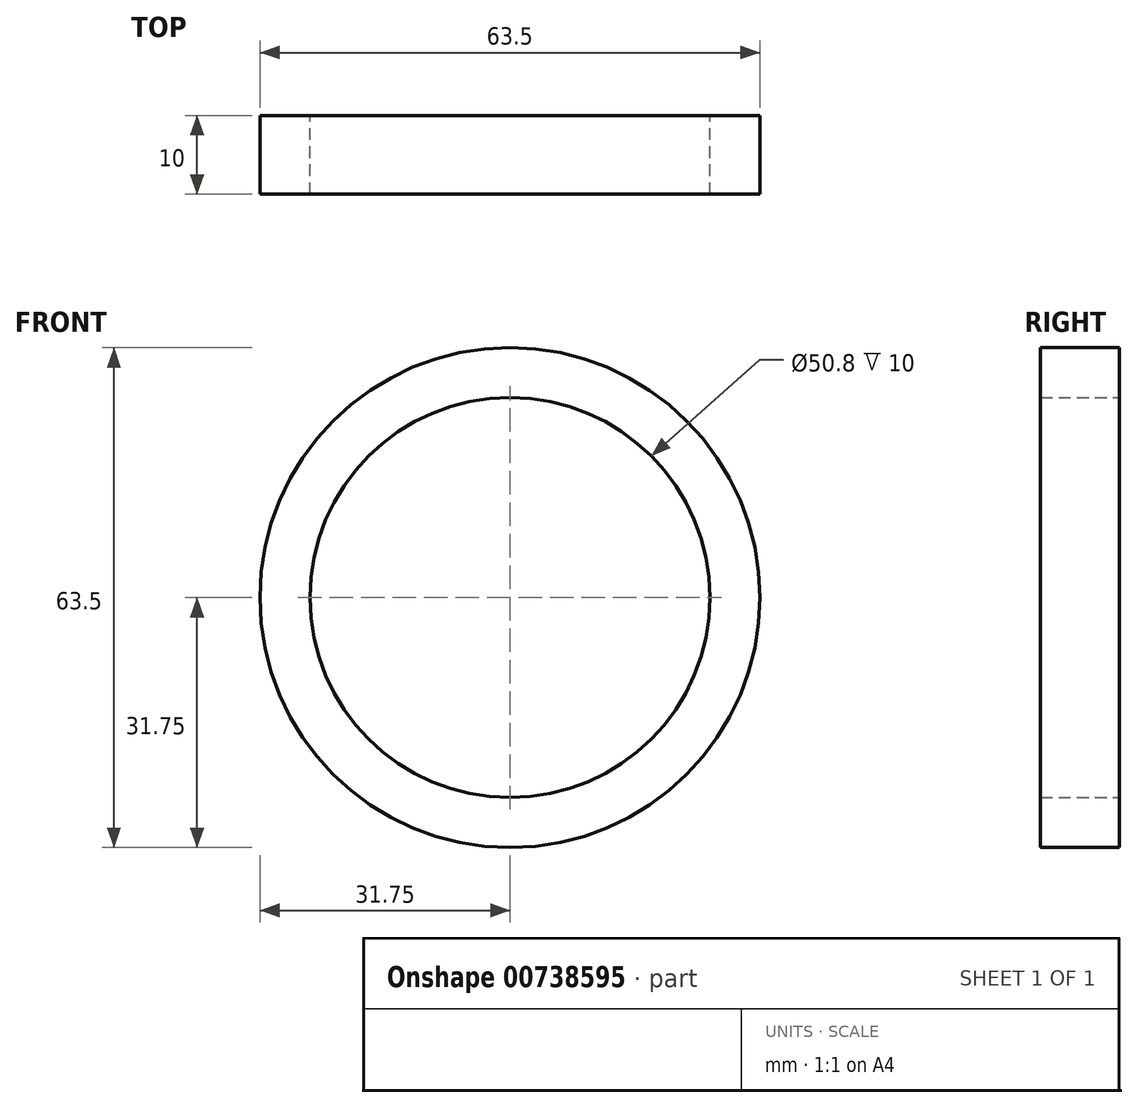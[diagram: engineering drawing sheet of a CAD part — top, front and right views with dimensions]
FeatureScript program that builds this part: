
annotation { "Feature Type Name" : "Feature", "Feature Type Description" : "" }
export const myFeature = defineFeature(function(context is Context, id is Id, definition is map)
    precondition{}
    {
        {
            var Q0;
            Q0=qCreatedBy(makeId("Front.planeOp"),FACE);
            var sketch = newSketch(context, id + "F0", { "sketchPlane" : qUnion([Q0])});
            skCircle(sketch, "E0", {"center": v(0, 0) * mm, "radius": 31.75 * mm});
            skCircle(sketch, "E1", {"center": v(0, 0) * mm, "radius": 25.4 * mm});
            skSolve(sketch);
        }
        {
            var Q0;
            Q0=makeQuery(id+"F0.imprint","IMPRINT",FACE,{"disambiguationData":[TD([[makeQuery(id+"F0.imprint","IMPRINT",EDGE,{"derivedFrom":sQuery(id+"F0.wireOp",EDGE,"E0")}),1.0]])]});
            extrude(context, id + "F1", {"entities" : qUnion([Q0]), "depth" : 10 * mm, "offsetDistance" : 25.4 * mm});
        }
    });
